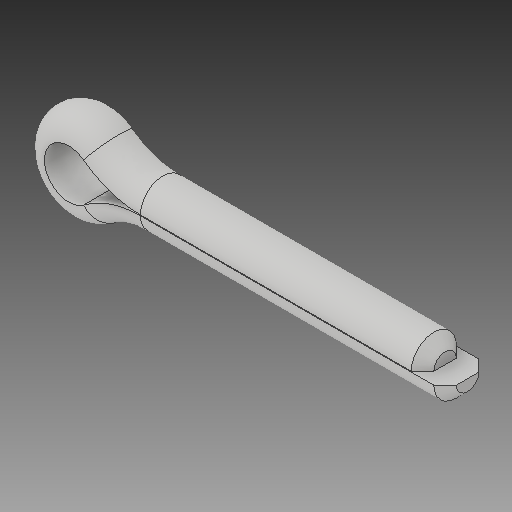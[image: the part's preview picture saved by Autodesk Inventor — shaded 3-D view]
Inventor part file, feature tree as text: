
AUTODESK INVENTOR PART (.ipt)
format: ipt  version: 2017 (Build 210142000, 142)  size: 128,512 bytes
history: native  units: mm
features: chamfer x1
ambient origin geometry x8: Origin, YZ Plane, XZ Plane, XY Plane, X Axis, Y Axis, Z Axis, Center Point
bodies: Solid1 (feature_tree)
feature tree (1):
  chamfer  "Chamfer1"  [1 undecoded]
note: 1 required parameter value undecoded (feature->parameter linkage not recoverable at this tier; creation-order binding heuristic only, values carry confidence <= 0.55)
